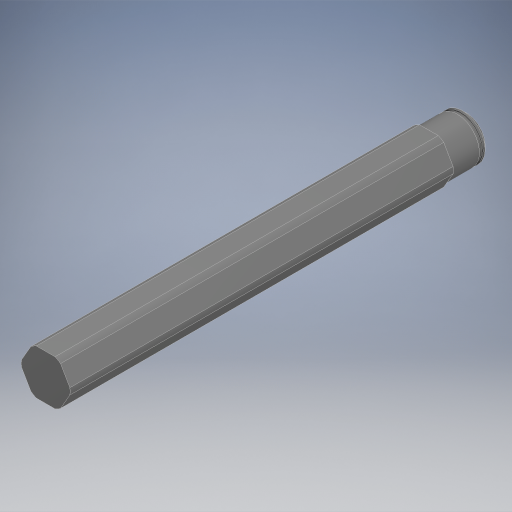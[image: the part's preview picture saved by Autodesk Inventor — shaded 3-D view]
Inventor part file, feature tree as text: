
AUTODESK INVENTOR PART (.ipt)
format: ipt  version: 2024.2 (Build 282272000, 272)  size: 335,360 bytes
history: native  units: in
note: dims shown in document units (in); Inventor stores cm internally (conversion verified against a paired STEP export)
features: projected_geometry x13, extrude x1, sketch x1, other x1
ambient origin geometry x8: Origin, YZ Plane, XZ Plane, XY Plane, X Axis, Y Axis, Z Axis, Center Point
bodies: Solid1 (feature_tree)
feature tree (16):
  extrude  "Extrusion1"  Depth=0.5in
  sketch  "Sketch1"  dims[d0=2.25in d1=0.0in d2=0.5in d3=1.9685in]
  projected_geometry  "Projected Loop1"
  projected_geometry  "Projected Loop2"
  projected_geometry  "Projected Loop3"
  projected_geometry  "Projected Loop4"
  projected_geometry  "Projected Loop5"
  projected_geometry  "Projected Loop6"
  projected_geometry  "Projected Loop7"
  projected_geometry  "Projected Loop8"
  projected_geometry  "Projected Loop9"
  projected_geometry  "Projected Loop10"
  projected_geometry  "Projected Loop11"
  projected_geometry  "Projected Loop12"
  projected_geometry  "Projected Loop13"
  other  "Cut-Extrude1"
